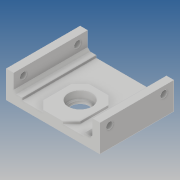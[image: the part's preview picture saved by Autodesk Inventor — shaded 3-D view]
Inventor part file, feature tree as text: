
AUTODESK INVENTOR PART (.ipt)
format: ipt  version: 2019 (Build 230136000, 136)  size: 159,232 bytes
history: native  units: mm
features: other x3, sketch x3, extrude x2, projected_geometry x2, hole x1, chamfer x1
ambient origin geometry x8: Origin, YZ Plane, XZ Plane, XY Plane, X Axis, Y Axis, Z Axis, Center Point
bodies: Solide1 (feature_tree)
feature tree (12):
  other  "base_cloison.ipt"
  extrude  "Extrusion1"  Depth=10.0mm
  hole  "Perçage1"  [1 undecoded]
  extrude  "Extrusion2"  Depth=22.0mm
  chamfer  "Chanfrein1"  Distance=2.0mm
  other  "Solide1::base_cloison.ipt"
  other  "FonctionRepérage1"
  sketch  "Esquisse2"
  sketch  "Esquisse3"
  projected_geometry  "Boucle projetée1"
  sketch  "Esquisse4"
  projected_geometry  "Boucle projetée2"
note: 1 required parameter value undecoded (feature->parameter linkage not recoverable at this tier; creation-order binding heuristic only, values carry confidence <= 0.55)
